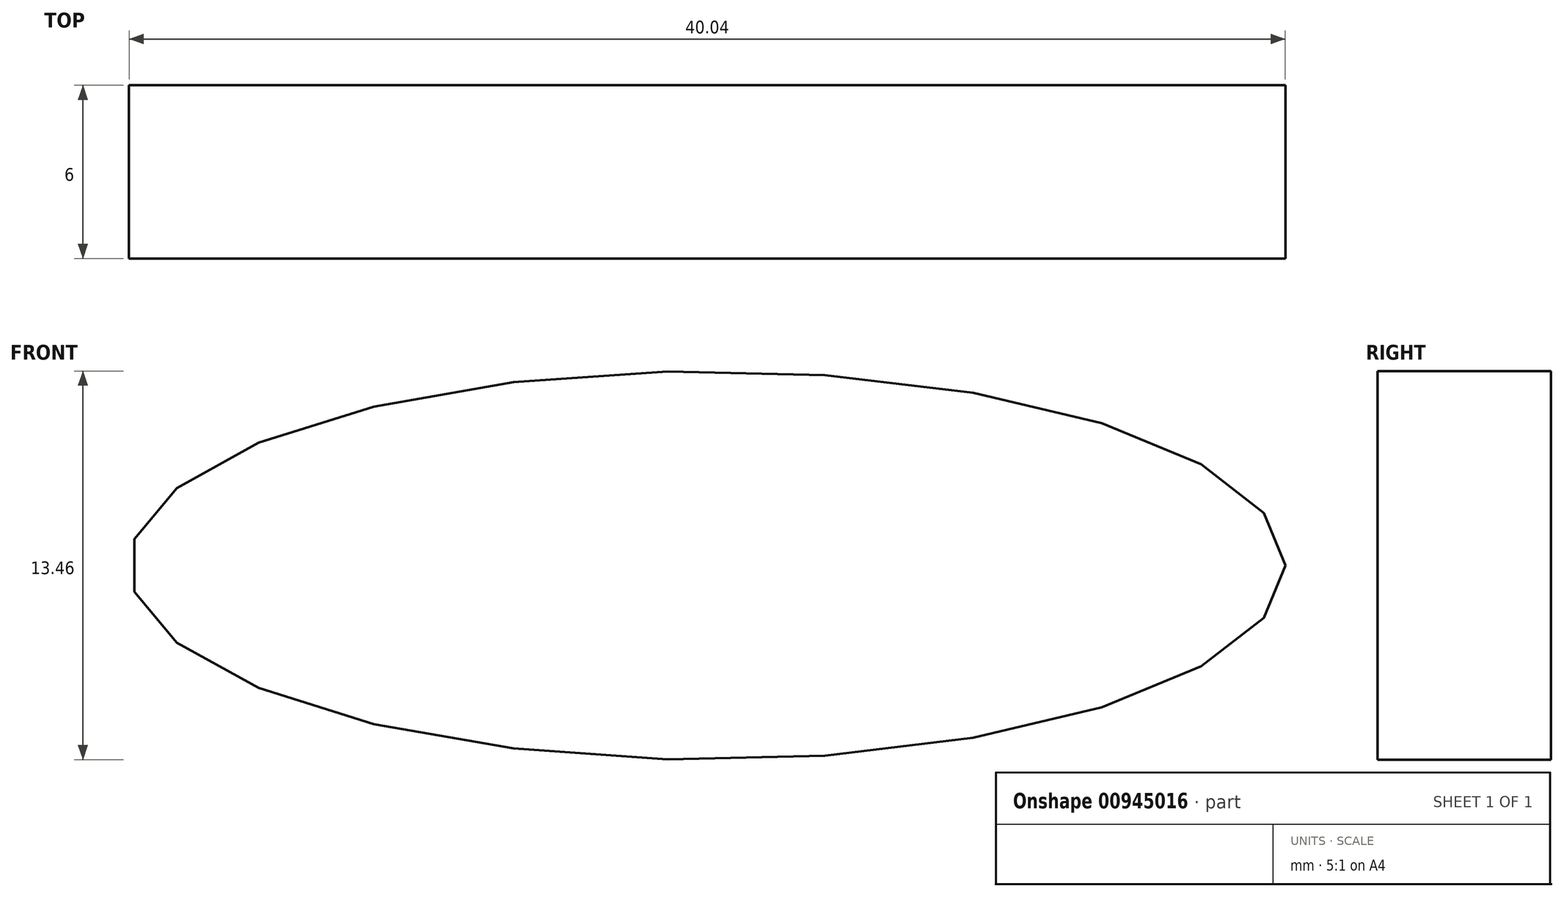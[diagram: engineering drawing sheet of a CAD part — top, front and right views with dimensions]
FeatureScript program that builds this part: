
annotation { "Feature Type Name" : "Feature", "Feature Type Description" : "" }
export const myFeature = defineFeature(function(context is Context, id is Id, definition is map)
    precondition{}
    {
        {
            var Q0;
            Q0=qCreatedBy(makeId("Front.planeOp"),FACE);
            var sketch = newSketch(context, id + "F0", { "sketchPlane" : qUnion([Q0])});
            skEllipse(sketch, "E0", {"center": v(0, 0) * mm, "majorRadius": 20.02 * mm, "minorRadius": 6.73 * mm, "majorAxis": v(1, 0)});
            skSolve(sketch);
        }
        {
            var Q0;
            Q0 = qSketchRegion(id + "F0", true);
            extrude(context, id + "F1", {"entities" : qUnion([Q0]), "depth" : 6 * mm, "offsetDistance" : 25 * mm});
        }
    });
